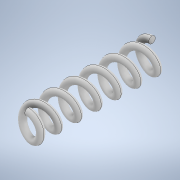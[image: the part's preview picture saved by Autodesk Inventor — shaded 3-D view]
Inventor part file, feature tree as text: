
AUTODESK INVENTOR PART (.ipt)
format: ipt  version: 2021 (Build 250183000, 183)  size: 436,736 bytes
history: native  units: in
note: dims shown in document units (in); Inventor stores cm internally (conversion verified against a paired STEP export)
features: helix x1, sketch x1
ambient origin geometry x8: Origin, YZ Plane, XZ Plane, XY Plane, X Axis, Y Axis, Z Axis, Center Point
bodies: Solid1 (feature_tree)
feature tree (2):
  helix  "Coil1"  [1 undecoded]
  sketch  "Sketch2"  dims[d1=0.0469in d2=1.0in d3=0.465in d4=2.3622in d5=0.0in d6=90.0deg d7=90.0deg d8=90.0deg d9=90.0deg]
note: 1 required parameter value undecoded (feature->parameter linkage not recoverable at this tier; creation-order binding heuristic only, values carry confidence <= 0.55)
